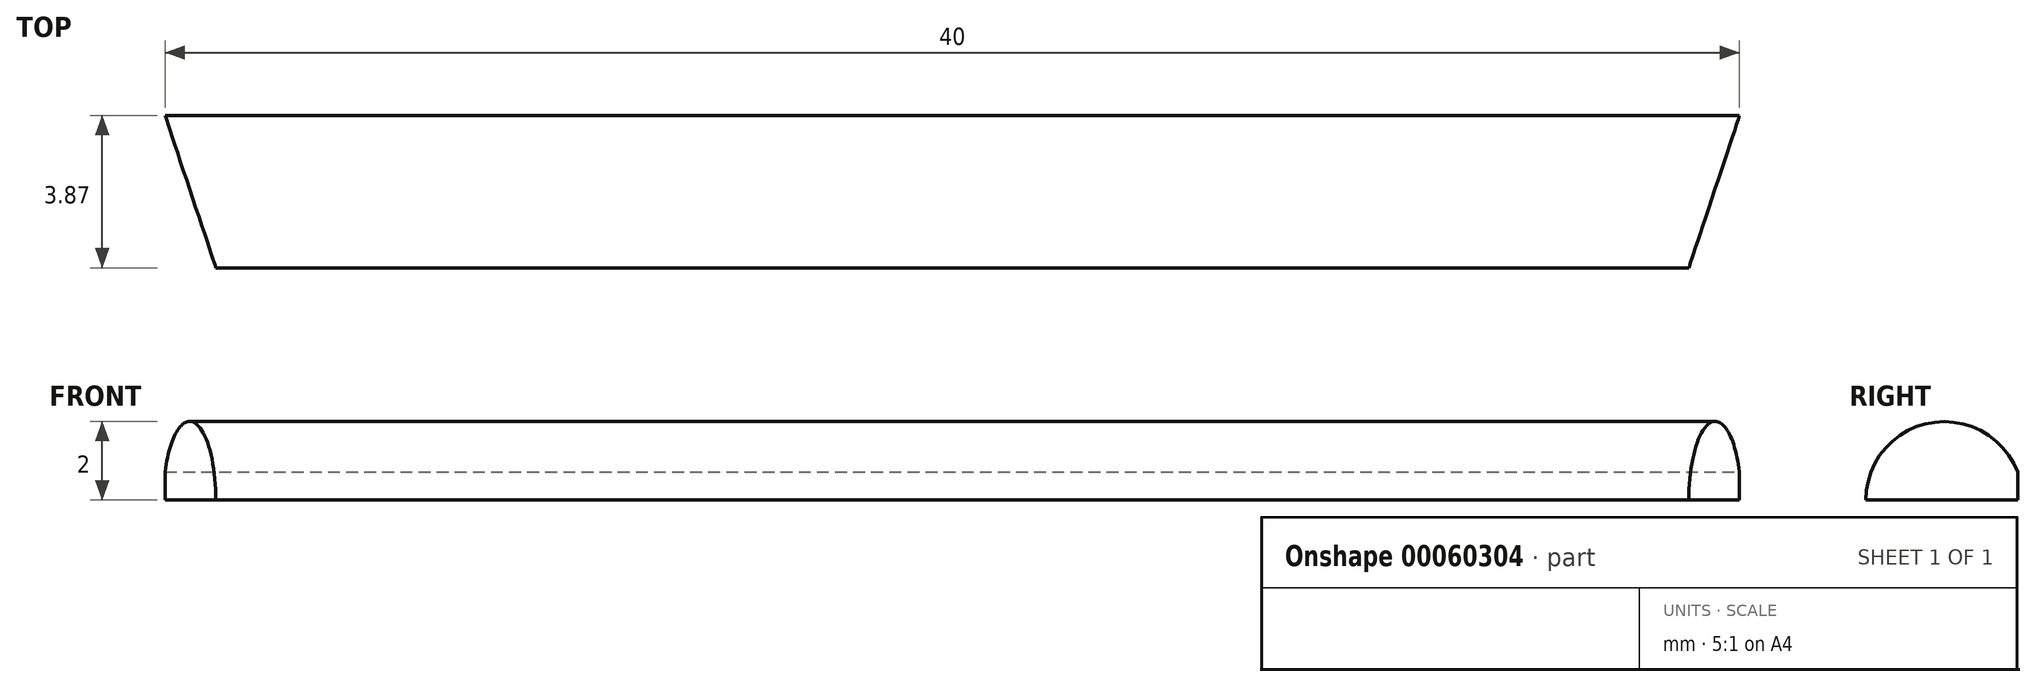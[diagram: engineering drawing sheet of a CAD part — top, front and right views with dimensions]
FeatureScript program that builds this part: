
annotation { "Feature Type Name" : "Feature", "Feature Type Description" : "" }
export const myFeature = defineFeature(function(context is Context, id is Id, definition is map)
    precondition{}
    {
        {
            var Q0;
            Q0=qCreatedBy(makeId("Top.planeOp"),FACE);
            var sketch = newSketch(context, id + "F0", { "sketchPlane" : qUnion([Q0])});
            skLineSegment(sketch, "E0.bottom", {"start": v(-20, 10.6) * mm, "end": v(20, 10.6) * mm});
            skLineSegment(sketch, "E0.top", {"start": v(-20, -10.6) * mm, "end": v(20, -10.6) * mm});
            skLineSegment(sketch, "E0.left", {"start": v(-20, 10.6) * mm, "end": v(-20, -10.6) * mm});
            skLineSegment(sketch, "E0.right", {"start": v(20, 10.6) * mm, "end": v(20, -10.6) * mm});
            skLineSegment(sketch, "E1", {"start": v(0, 10.6) * mm, "end": v(0, -10.6) * mm, "construction": true});
            skCircle(sketch, "E2", {"center": v(-8, -7.5) * mm, "radius": 1.75 * mm});
            skCircle(sketch, "E3", {"center": v(8, -7.5) * mm, "radius": 1.75 * mm});
            skLineSegment(sketch, "E4", {"start": v(-20, -7.5) * mm, "end": v(20, -7.5) * mm, "construction": true});
            skLineSegment(sketch, "E5", {"start": v(-20, 7.5) * mm, "end": v(20, 7.5) * mm, "construction": true});
            skCircle(sketch, "E6", {"center": v(-8, 7.5) * mm, "radius": 1.75 * mm});
            skCircle(sketch, "E7", {"center": v(8, 7.5) * mm, "radius": 1.75 * mm});
            skLineSegment(sketch, "E8", {"start": v(20, 0) * mm, "end": v(-20, 0) * mm, "construction": true});
            skLineSegment(sketch, "E9", {"start": v(8, 10.6) * mm, "end": v(8, -10.6) * mm, "construction": true});
            skLineSegment(sketch, "E10", {"start": v(-8, 10.6) * mm, "end": v(-8, -10.6) * mm, "construction": true});
            skCircle(sketch, "E11", {"center": v(-8, -7.5) * mm, "radius": 3 * mm});
            skCircle(sketch, "E12.MirrorC", {"center": v(8, -7.5) * mm, "radius": 3 * mm});
            skCircle(sketch, "E13.MirrorC", {"center": v(-8, 7.5) * mm, "radius": 3 * mm});
            skCircle(sketch, "E14.MirrorC", {"center": v(8, 7.5) * mm, "radius": 3 * mm});
            skPoint(sketch, "E15.MirrorCS.start.orphan", {"position": v(20, -10) * mm});
            skLineSegment(sketch, "E16", {"start": v(0, -40.6) * mm, "end": v(10, -40.6) * mm});
            skLineSegment(sketch, "E17.MirrorCS", {"start": v(0, -40.6) * mm, "end": v(-10, -40.6) * mm});
            skLineSegment(sketch, "E18", {"start": v(20, -10.6) * mm, "end": v(10, -40.6) * mm});
            skLineSegment(sketch, "E19", {"start": v(-20, -10.6) * mm, "end": v(-10, -40.6) * mm});
            skLineSegment(sketch, "E20", {"start": v(0, -10.6) * mm, "end": v(0, -40.6) * mm, "construction": true});
            skCircle(sketch, "E21", {"center": v(0, -18.1) * mm, "radius": 2.75 * mm});
            skCircle(sketch, "E22", {"center": v(0, -33.1) * mm, "radius": 2.75 * mm});
            skSolve(sketch);
        }
        {
            var Q0;
            Q0=makeQuery(id+"F0.imprint","IMPRINT",FACE,{"disambiguationData":[TD([[makeQuery(id+"F0.imprint","IMPRINT",EDGE,{"derivedFrom":sQuery(id+"F0.wireOp",EDGE,"E0.bottom")}),-1.0]])]});
            var Q1;
            Q1=makeQuery(id+"F0.imprint","IMPRINT",FACE,{"disambiguationData":[TD([[makeQuery(id+"F0.imprint","IMPRINT",EDGE,{"derivedFrom":sQuery(id+"F0.wireOp",EDGE,"E0.top")}),-1.0]])]});
            extrude(context, id + "F1", {"entities" : qUnion([Q0, Q1]), "depth" : 6 * mm});
        }
        {
            var Q0;
            Q0=makeQuery(id+"F0.imprint","IMPRINT",FACE,{"disambiguationData":[TD([[makeQuery(id+"F0.imprint","IMPRINT",EDGE,{"derivedFrom":sQuery(id+"F0.wireOp",EDGE,"E6")}),-1.0]])]});
            var Q1;
            Q1=makeQuery(id+"F0.imprint","IMPRINT",FACE,{"disambiguationData":[TD([[makeQuery(id+"F0.imprint","IMPRINT",EDGE,{"derivedFrom":sQuery(id+"F0.wireOp",EDGE,"E7")}),-1.0]])]});
            var Q2;
            Q2=makeQuery(id+"F0.imprint","IMPRINT",FACE,{"disambiguationData":[TD([[makeQuery(id+"F0.imprint","IMPRINT",EDGE,{"derivedFrom":sQuery(id+"F0.wireOp",EDGE,"E3")}),-1.0]])]});
            var Q3;
            {var subQ0=sQuery(id+"F0.wireOp",EDGE,"E12.MirrorC");var subQ1=sQuery(id+"F0.wireOp",EDGE,"E0.top");var subQ2=makeQuery(id+"F0.imprint","INTERSECT",VERTEX,{"disambiguationData":[OD(0.0)],"derivedFrom":[subQ1,subQ0]});Q3=makeQuery(id+"F0.imprint","IMPRINT",FACE,{"disambiguationData":[TD([[makeQuery(id+"F0.imprint","IMPRINT",EDGE,{"disambiguationData":[TD([[subQ2,-1.0]])],"derivedFrom":subQ1}),-1.0]])]});}
            var Q4;
            Q4=makeQuery(id+"F0.imprint","IMPRINT",FACE,{"disambiguationData":[TD([[makeQuery(id+"F0.imprint","IMPRINT",EDGE,{"derivedFrom":sQuery(id+"F0.wireOp",EDGE,"E2")}),-1.0]])]});
            var Q5;
            {var subQ0=sQuery(id+"F0.wireOp",EDGE,"E11");var subQ1=sQuery(id+"F0.wireOp",EDGE,"E0.top");var subQ2=makeQuery(id+"F0.imprint","INTERSECT",VERTEX,{"disambiguationData":[OD(0.0)],"derivedFrom":[subQ1,subQ0]});Q5=makeQuery(id+"F0.imprint","IMPRINT",FACE,{"disambiguationData":[TD([[makeQuery(id+"F0.imprint","IMPRINT",EDGE,{"disambiguationData":[TD([[subQ2,-1.0]])],"derivedFrom":subQ1}),-1.0]])]});}
            var Q6;
            {var subQ0=sQuery(id+"F0.wireOp",EDGE,"E13.MirrorC");var subQ1=sQuery(id+"F0.wireOp",EDGE,"E0.bottom");var subQ2=makeQuery(id+"F0.imprint","INTERSECT",VERTEX,{"disambiguationData":[OD(0.0)],"derivedFrom":[subQ1,subQ0]});Q6=makeQuery(id+"F0.imprint","IMPRINT",FACE,{"disambiguationData":[TD([[makeQuery(id+"F0.imprint","IMPRINT",EDGE,{"disambiguationData":[TD([[subQ2,-1.0]])],"derivedFrom":subQ1}),1.0]])]});}
            var Q7;
            {var subQ0=sQuery(id+"F0.wireOp",EDGE,"E14.MirrorC");var subQ1=sQuery(id+"F0.wireOp",EDGE,"E0.bottom");var subQ2=makeQuery(id+"F0.imprint","INTERSECT",VERTEX,{"disambiguationData":[OD(0.0)],"derivedFrom":[subQ1,subQ0]});Q7=makeQuery(id+"F0.imprint","IMPRINT",FACE,{"disambiguationData":[TD([[makeQuery(id+"F0.imprint","IMPRINT",EDGE,{"disambiguationData":[TD([[subQ2,-1.0]])],"derivedFrom":subQ1}),1.0]])]});}
            extrude(context, id + "F2", {"entities" : qUnion([Q0, Q1, Q2, Q3, Q4, Q5, Q6, Q7]), "operationType" : NewBodyOperationType.ADD, "depth" : 2.5 * mm});
        }
        {
            var Q0;
            Q0=makeQuery(id+"F1.opExtrude","SWEPT_FACE",FACE,{"disambiguationData":[OSD([sQuery(id+"F0.wireOp",EDGE,"E0.right")])]});
            var sketch = newSketch(context, id + "F3", { "sketchPlane" : qUnion([Q0])});
            skLineSegment(sketch, "E23.bottom", {"start": v(10.6, 6) * mm, "end": v(-40.6, 6) * mm});
            skLineSegment(sketch, "E23.top", {"start": v(10.6, 0) * mm, "end": v(-40.6, 0) * mm});
            skLineSegment(sketch, "E23.left", {"start": v(10.6, 6) * mm, "end": v(10.6, 0) * mm});
            skLineSegment(sketch, "E23.right", {"start": v(-40.6, 6) * mm, "end": v(-40.6, 0) * mm});
            skCircle(sketch, "E24", {"center": v(0, 0) * mm, "radius": 2 * mm});
            skLineSegment(sketch, "E25", {"start": v(-25.18, 6) * mm, "end": v(-25.18, 0) * mm, "construction": true});
            skLineSegment(sketch, "E26", {"start": v(-12.47, 6) * mm, "end": v(-12.47, 0) * mm, "construction": true});
            skCircle(sketch, "E27", {"center": v(-12.47, 0) * mm, "radius": 2 * mm});
            skCircle(sketch, "E28", {"center": v(-25.18, 0) * mm, "radius": 2 * mm});
            skSolve(sketch);
        }
        {
            var Q0;
            {var subQ0=sQuery(id+"F3.wireOp",EDGE,"E28");var subQ1=sQuery(id+"F3.wireOp",EDGE,"E23.top");var subQ2=makeQuery(id+"F3.imprint","INTERSECT",VERTEX,{"disambiguationData":[OD(0.0)],"derivedFrom":[subQ1,subQ0]});Q0=makeQuery(id+"F3.imprint","IMPRINT",FACE,{"disambiguationData":[TD([[makeQuery(id+"F3.imprint","IMPRINT",EDGE,{"disambiguationData":[TD([[subQ2,-1.0]])],"derivedFrom":subQ1}),1.0]])]});}
            var Q1;
            {var subQ0=sQuery(id+"F3.wireOp",EDGE,"E28");var subQ1=sQuery(id+"F3.wireOp",EDGE,"E23.top");var subQ2=makeQuery(id+"F3.imprint","INTERSECT",VERTEX,{"disambiguationData":[OD(0.0)],"derivedFrom":[subQ1,subQ0]});Q1=makeQuery(id+"F3.imprint","IMPRINT",FACE,{"disambiguationData":[TD([[makeQuery(id+"F3.imprint","IMPRINT",EDGE,{"disambiguationData":[TD([[subQ2,-1.0]])],"derivedFrom":subQ1}),-1.0]])]});}
            var Q2;
            {var subQ0=sQuery(id+"F3.wireOp",EDGE,"E23.top");var subQ2=sQuery(id+"F3.wireOp",EDGE,"E27");var subQ3=makeQuery(id+"F3.imprint","INTERSECT",VERTEX,{"disambiguationData":[OD(0.0)],"derivedFrom":[subQ0,subQ2]});Q2=makeQuery(id+"F3.imprint","IMPRINT",FACE,{"disambiguationData":[TD([[makeQuery(id+"F3.imprint","IMPRINT",EDGE,{"disambiguationData":[TD([[subQ3,-1.0]])],"derivedFrom":subQ2}),1.0]])]});}
            var Q3;
            {var subQ0=sQuery(id+"F3.wireOp",EDGE,"E23.top");var subQ3=sQuery(id+"F3.wireOp",EDGE,"E27");var subQ4=makeQuery(id+"F3.imprint","INTERSECT",VERTEX,{"disambiguationData":[OD(0.0)],"derivedFrom":[subQ0,subQ3]});Q3=makeQuery(id+"F3.imprint","IMPRINT",FACE,{"disambiguationData":[TD([[makeQuery(id+"F3.imprint","IMPRINT",EDGE,{"disambiguationData":[TD([[subQ4,1.0]])],"derivedFrom":subQ0}),-1.0]])]});}
            var Q4;
            {var subQ0=sQuery(id+"F3.wireOp",EDGE,"E23.top");var subQ3=sQuery(id+"F3.wireOp",EDGE,"E27");var subQ4=makeQuery(id+"F3.imprint","INTERSECT",VERTEX,{"disambiguationData":[OD(1.0)],"derivedFrom":[subQ0,subQ3]});Q4=makeQuery(id+"F3.imprint","IMPRINT",FACE,{"disambiguationData":[TD([[makeQuery(id+"F3.imprint","IMPRINT",EDGE,{"disambiguationData":[TD([[subQ4,-1.0]])],"derivedFrom":subQ0}),-1.0]])]});}
            var Q5;
            {var subQ0=sQuery(id+"F3.wireOp",EDGE,"E24");var subQ1=sQuery(id+"F3.wireOp",EDGE,"E23.top");var subQ2=makeQuery(id+"F3.imprint","INTERSECT",VERTEX,{"disambiguationData":[OD(0.0)],"derivedFrom":[subQ1,subQ0]});Q5=makeQuery(id+"F3.imprint","IMPRINT",FACE,{"disambiguationData":[TD([[makeQuery(id+"F3.imprint","IMPRINT",EDGE,{"disambiguationData":[TD([[subQ2,-1.0]])],"derivedFrom":subQ1}),1.0]])]});}
            var Q6;
            {var subQ0=sQuery(id+"F3.wireOp",EDGE,"E24");var subQ1=sQuery(id+"F3.wireOp",EDGE,"E23.top");var subQ2=makeQuery(id+"F3.imprint","INTERSECT",VERTEX,{"disambiguationData":[OD(0.0)],"derivedFrom":[subQ1,subQ0]});Q6=makeQuery(id+"F3.imprint","IMPRINT",FACE,{"disambiguationData":[TD([[makeQuery(id+"F3.imprint","IMPRINT",EDGE,{"disambiguationData":[TD([[subQ2,-1.0]])],"derivedFrom":subQ1}),-1.0]])]});}
            extrude(context, id + "F4", {"entities" : qUnion([Q0, Q1, Q2, Q3, Q4, Q5, Q6]), "operationType" : NewBodyOperationType.REMOVE, "oppositeDirection" : true, "depth" : 52.1 * mm});
        }
    });
